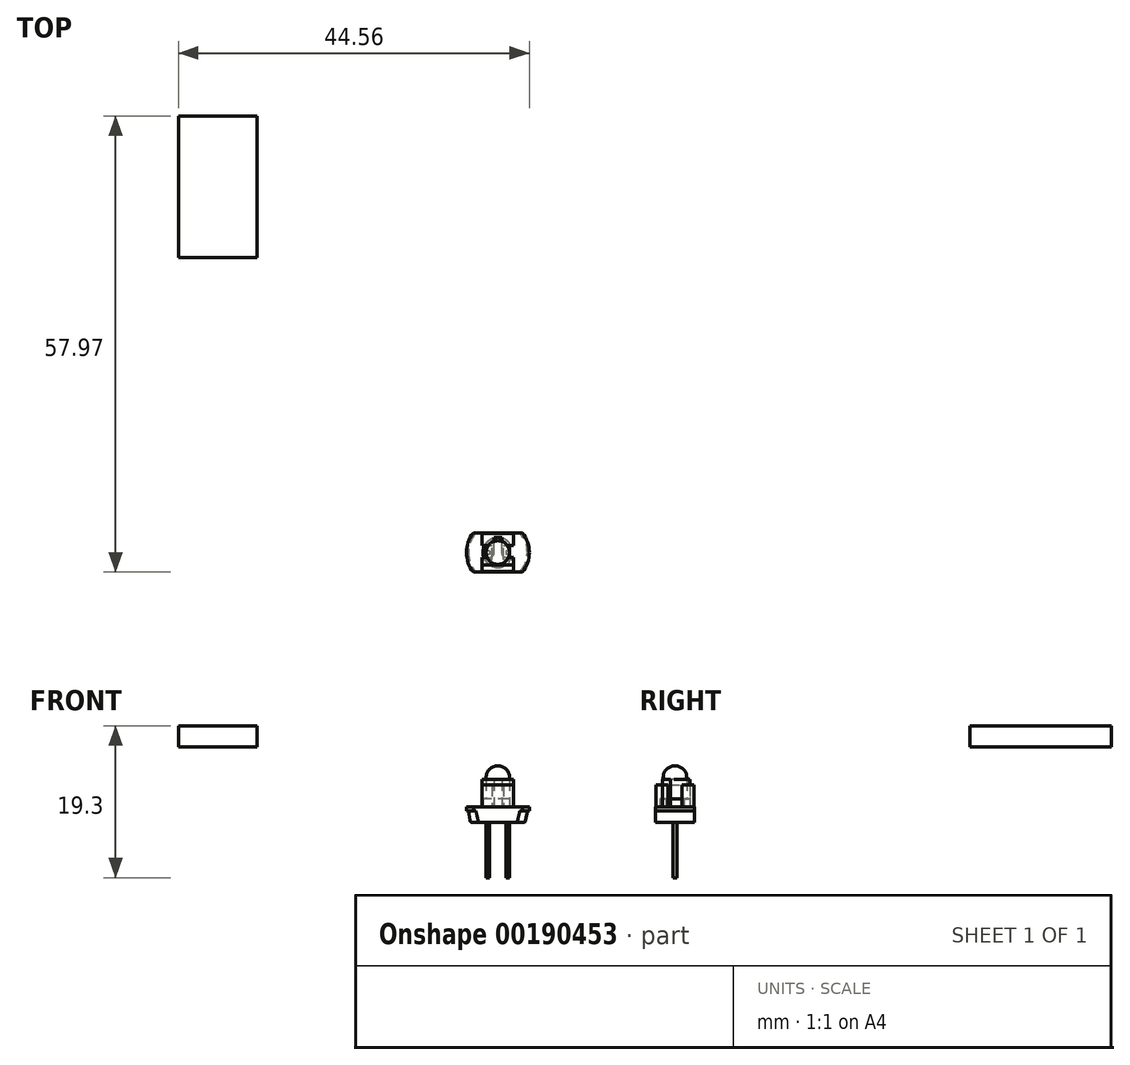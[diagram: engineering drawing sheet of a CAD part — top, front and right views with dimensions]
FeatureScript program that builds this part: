
annotation { "Feature Type Name" : "Feature", "Feature Type Description" : "" }
export const myFeature = defineFeature(function(context is Context, id is Id, definition is map)
    precondition{}
    {
        {
            var Q0;
            Q0=qCreatedBy(makeId("Front.planeOp"),FACE);
            var sketch = newSketch(context, id + "F0", { "sketchPlane" : qUnion([Q0])});
            skLineSegment(sketch, "E0", {"start": v(0, 10.98) * mm, "end": v(0, -8.22) * mm, "construction": true});
            skSolve(sketch);
        }
        {
            var Q0;
            Q0=qCreatedBy(makeId("Top.planeOp"),FACE);
            cPlane(context, id + "F1", {"entities" : qUnion([Q0]), "cplaneType" : CPlaneType.OFFSET, "offset" : 2 * mm, "width" : 150 * mm, "height" : 150 * mm});
        }
        {
            var Q0;
            Q0=qCreatedBy(makeId("Top.planeOp"),FACE);
            var sketch = newSketch(context, id + "F2", { "sketchPlane" : qUnion([Q0])});
            skLineSegment(sketch, "E1", {"start": v(0, 8.57) * mm, "end": v(0, -6.8) * mm, "construction": true});
            skLineSegment(sketch, "E2", {"start": v(-7.73, 0) * mm, "end": v(6.61, 0) * mm, "construction": true});
            skLineSegment(sketch, "E3.bottom", {"start": v(-4.25, 1.75) * mm, "end": v(4.25, 1.75) * mm});
            skLineSegment(sketch, "E3.top", {"start": v(-4.25, -1.75) * mm, "end": v(4.25, -1.75) * mm});
            skLineSegment(sketch, "E3.left", {"start": v(-4.25, 1.75) * mm, "end": v(-4.25, -1.75) * mm});
            skLineSegment(sketch, "E3.right", {"start": v(4.25, 1.75) * mm, "end": v(4.25, -1.75) * mm});
            skSolve(sketch);
        }
        {
            var Q0;
            Q0=qSketchRegion(id+"F2",true);
            extrude(context, id + "F3", {"entities" : qUnion([Q0]), "depth" : 3.5 * mm});
        }
        {
            var Q0;
            Q0=makeQuery(id+"F3.opExtrude","CAP_FACE",FACE,{"disambiguationData":[OSD([sQuery(id+"F2.wireOp",EDGE,"E3.bottom"),sQuery(id+"F2.wireOp",EDGE,"E3.top"),sQuery(id+"F2.wireOp",EDGE,"E3.left"),sQuery(id+"F2.wireOp",EDGE,"E3.right")])],"isStart":false});
            var sketch = newSketch(context, id + "F4", { "sketchPlane" : qUnion([Q0])});
            skLineSegment(sketch, "E4.bottom", {"start": v(-1.75, 0.75) * mm, "end": v(-0.25, 0.75) * mm});
            skLineSegment(sketch, "E4.top", {"start": v(-1.75, -0.75) * mm, "end": v(-0.25, -0.75) * mm});
            skLineSegment(sketch, "E4.left", {"start": v(-1.75, 0.75) * mm, "end": v(-1.75, -0.75) * mm});
            skLineSegment(sketch, "E4.right", {"start": v(-0.25, 0.75) * mm, "end": v(-0.25, -0.75) * mm});
            skLineSegment(sketch, "E5", {"start": v(-2.91, 0) * mm, "end": v(1.63, 0) * mm, "construction": true});
            skSolve(sketch);
        }
        {
            var Q0;
            Q0=qSketchRegion(id+"F4",true);
            extrude(context, id + "F5", {"entities" : qUnion([Q0]), "operationType" : NewBodyOperationType.ADD, "depth" : 2 * mm});
        }
        {
            var Q0;
            Q0=makeQuery(id+"F3.opExtrude","CAP_FACE",FACE,{"disambiguationData":[OSD([sQuery(id+"F2.wireOp",EDGE,"E3.bottom"),sQuery(id+"F2.wireOp",EDGE,"E3.top"),sQuery(id+"F2.wireOp",EDGE,"E3.left"),sQuery(id+"F2.wireOp",EDGE,"E3.right")])],"isStart":true});
            var sketch = newSketch(context, id + "F6", { "sketchPlane" : qUnion([Q0])});
            skLineSegment(sketch, "E6.bottom", {"start": v(-2.8, 2.5) * mm, "end": v(-2.2, 2.5) * mm});
            skLineSegment(sketch, "E6.top", {"start": v(-2.8, 1.75) * mm, "end": v(-2.2, 1.75) * mm});
            skLineSegment(sketch, "E6.left", {"start": v(-2.8, 2.5) * mm, "end": v(-2.8, 1.75) * mm});
            skLineSegment(sketch, "E6.right", {"start": v(-2.2, 2.5) * mm, "end": v(-2.2, 1.75) * mm});
            skLineSegment(sketch, "E7.1.0.0", {"start": v(-0.3, 1.75) * mm, "end": v(0.3, 1.75) * mm});
            skLineSegment(sketch, "E7.1.0.1", {"start": v(-0.3, 2.5) * mm, "end": v(-0.3, 1.75) * mm});
            skLineSegment(sketch, "E7.1.0.2", {"start": v(0.3, 2.5) * mm, "end": v(0.3, 1.75) * mm});
            skLineSegment(sketch, "E7.1.0.3", {"start": v(-0.3, 2.5) * mm, "end": v(0.3, 2.5) * mm});
            skLineSegment(sketch, "E7.2.0.0", {"start": v(2.2, 1.75) * mm, "end": v(2.8, 1.75) * mm});
            skLineSegment(sketch, "E7.2.0.1", {"start": v(2.2, 2.5) * mm, "end": v(2.2, 1.75) * mm});
            skLineSegment(sketch, "E7.2.0.2", {"start": v(2.8, 2.5) * mm, "end": v(2.8, 1.75) * mm});
            skLineSegment(sketch, "E7.2.0.3", {"start": v(2.2, 2.5) * mm, "end": v(2.8, 2.5) * mm});
            skLineSegment(sketch, "E7.direction1", {"start": v(-2.8, 1.75) * mm, "end": v(-0.3, 1.75) * mm, "construction": true});
            skLineSegment(sketch, "E8", {"start": v(-2.83, 0) * mm, "end": v(2.14, 0) * mm, "construction": true});
            skLineSegment(sketch, "E9.0.MirrorCS", {"start": v(2.2, -2.5) * mm, "end": v(2.8, -2.5) * mm});
            skLineSegment(sketch, "E9.1.MirrorCS", {"start": v(-0.3, -2.5) * mm, "end": v(0.3, -2.5) * mm});
            skLineSegment(sketch, "E9.2.MirrorCS", {"start": v(-2.8, -2.5) * mm, "end": v(-2.2, -2.5) * mm});
            skLineSegment(sketch, "E9.3.MirrorCS", {"start": v(2.8, -2.5) * mm, "end": v(2.8, -1.75) * mm});
            skLineSegment(sketch, "E9.4.MirrorCS", {"start": v(2.2, -2.5) * mm, "end": v(2.2, -1.75) * mm});
            skLineSegment(sketch, "E9.5.MirrorCS", {"start": v(0.3, -2.5) * mm, "end": v(0.3, -1.75) * mm});
            skLineSegment(sketch, "E9.6.MirrorCS", {"start": v(-0.3, -2.5) * mm, "end": v(-0.3, -1.75) * mm});
            skLineSegment(sketch, "E9.7.MirrorCS", {"start": v(-2.2, -2.5) * mm, "end": v(-2.2, -1.75) * mm});
            skLineSegment(sketch, "E9.8.MirrorCS", {"start": v(-2.8, -2.5) * mm, "end": v(-2.8, -1.75) * mm});
            skLineSegment(sketch, "E9.9.MirrorCS", {"start": v(2.2, -1.75) * mm, "end": v(2.8, -1.75) * mm});
            skLineSegment(sketch, "E9.10.MirrorCS", {"start": v(-2.8, -1.75) * mm, "end": v(-2.2, -1.75) * mm});
            skLineSegment(sketch, "E9.11.MirrorCS", {"start": v(-0.3, -1.75) * mm, "end": v(0.3, -1.75) * mm});
            skSolve(sketch);
        }
        {
            var Q0;
            Q0=qSketchRegion(id+"F6",true);
            extrude(context, id + "F7", {"entities" : qUnion([Q0]), "operationType" : NewBodyOperationType.ADD, "oppositeDirection" : true, "depth" : 0.3 * mm});
        }
        {
            var Q0;
            Q0=makeQuery(id+"F3.opExtrude","SWEPT_BODY",BODY,{"disambiguationData":[OSD([sQuery(id+"F2.wireOp",EDGE,"E3.bottom"),sQuery(id+"F2.wireOp",EDGE,"E3.top"),sQuery(id+"F2.wireOp",EDGE,"E3.left"),sQuery(id+"F2.wireOp",EDGE,"E3.right")])]});
            transform(context, id + "F8", {"entities" : qUnion([Q0]), "transformType" : TransformType.TRANSLATION_3D, "dx" : -23 * mm, "dy" : 46.3 * mm, "dz" : 7.6 * mm, "makeCopy" : false});
        }
        {
            var Q0;
            Q0=qCreatedBy(makeId("Front.planeOp"),FACE);
            var sketch = newSketch(context, id + "F9", { "sketchPlane" : qUnion([Q0])});
            skLineSegment(sketch, "E10", {"start": v(0, 0) * mm, "end": v(4, 0) * mm});
            skLineSegment(sketch, "E11", {"start": v(4, 0) * mm, "end": v(4, -0.5) * mm});
            skLineSegment(sketch, "E12", {"start": v(4, -0.5) * mm, "end": v(3.75, -0.5) * mm});
            skLineSegment(sketch, "E13", {"start": v(3.75, -0.5) * mm, "end": v(3.54, -1.75) * mm});
            skLineSegment(sketch, "E14", {"start": v(3.25, -2) * mm, "end": v(0, -2) * mm});
            skLineSegment(sketch, "E15", {"start": v(0, -2) * mm, "end": v(0, 0) * mm});
            skPoint(sketch, "E16.visualSharp", {"position": v(3.5, -2) * mm});
            skArc(sketch, "E16.filletArc", {"start": v(3.25, -2) * mm, "mid": v(3.44, -1.93) * mm, "end": v(3.54, -1.75) * mm});
            skSolve(sketch);
        }
        {
            var Q0;
            Q0=qSketchRegion(id+"F9",true);
            var Q1;
            Q1=sQuery(id+"F9.wireOp",EDGE,"E15");
            revolve(context, id + "F10", {"entities" : qUnion([Q0]), "axis" : qUnion([Q1]), "revolveType" : RevolveType.FULL});
        }
        {
            var Q0;
            Q0=qCreatedBy(makeId("Front.planeOp"),FACE);
            var sketch = newSketch(context, id + "F11", { "sketchPlane" : qUnion([Q0])});
            skLineSegment(sketch, "E17", {"start": v(0, 0) * mm, "end": v(4, 0) * mm});
            skLineSegment(sketch, "E18", {"start": v(4, 0) * mm, "end": v(4, -0.5) * mm});
            skLineSegment(sketch, "E19", {"start": v(4, -0.5) * mm, "end": v(3.75, -0.5) * mm});
            skLineSegment(sketch, "E20", {"start": v(3.75, -0.5) * mm, "end": v(3.64, -0.68) * mm});
            skLineSegment(sketch, "E21", {"start": v(0, 0) * mm, "end": v(0, -2) * mm});
            skLineSegment(sketch, "E22", {"start": v(0, -2) * mm, "end": v(0.5, -2) * mm});
            skArc(sketch, "E23", {"start": v(0.5, -2) * mm, "mid": v(2.2, -1.66) * mm, "end": v(3.64, -0.68) * mm});
            skSolve(sketch);
        }
        {
            var Q0;
            Q0=qSketchRegion(id+"F11",true);
            var Q1;
            Q1=sQuery(id+"F11.wireOp",EDGE,"E21");
            revolve(context, id + "F12", {"entities" : qUnion([Q0]), "axis" : qUnion([Q1]), "revolveType" : RevolveType.FULL});
        }
        {
            var Q0;
            Q0=makeQuery(id+"F12.opRevolve","SWEPT_BODY",BODY,{"disambiguationData":[OSD([sQuery(id+"F11.wireOp",EDGE,"E17"),sQuery(id+"F11.wireOp",EDGE,"E18"),sQuery(id+"F11.wireOp",EDGE,"E19"),sQuery(id+"F11.wireOp",EDGE,"E20"),sQuery(id+"F11.wireOp",EDGE,"E21"),sQuery(id+"F11.wireOp",EDGE,"E22"),sQuery(id+"F11.wireOp",EDGE,"E23")])]});
            transform(context, id + "F13", {"entities" : qUnion([Q0]), "transformType" : TransformType.COPY});
        }
        {
            var Q0;
            Q0=makeQuery(id+"F13.opPattern","COPY",FACE,{"derivedFrom":makeQuery(id+"F12.opRevolve","SWEPT_FACE",FACE,{"disambiguationData":[OSD([sQuery(id+"F11.wireOp",EDGE,"E17")])]}),"instanceName":"1"});
            var sketch = newSketch(context, id + "F14", { "sketchPlane" : qUnion([Q0])});
            skLineSegment(sketch, "E24", {"start": v(-3.12, 2.5) * mm, "end": v(3.12, 2.5) * mm});
            skLineSegment(sketch, "E25", {"start": v(-3.12, -2.5) * mm, "end": v(3.12, -2.5) * mm});
            skLineSegment(sketch, "E26", {"start": v(0, 0) * mm, "end": v(3.07, 0) * mm, "construction": true});
            skArc(sketch, "E27.0", {"start": v(-3.12, 2.5) * mm, "mid": v(-4, 0) * mm, "end": v(-3.12, -2.5) * mm});
            skArc(sketch, "E28.trimOffspring", {"start": v(3.12, -2.5) * mm, "mid": v(4, 0) * mm, "end": v(3.12, 2.5) * mm});
            skSolve(sketch);
        }
        {
            var Q0;
            Q0=qSketchRegion(id+"F14",true);
            extrude(context, id + "F15", {"entities" : qUnion([Q0]), "operationType" : NewBodyOperationType.INTERSECT, "oppositeDirection" : true, "depth" : 25 * mm});
        }
        {
            var Q0;
            Q0=qCreatedBy(makeId("Front.planeOp"),FACE);
            var sketch = newSketch(context, id + "F16", { "sketchPlane" : qUnion([Q0])});
            skLineSegment(sketch, "E29", {"start": v(0, 0) * mm, "end": v(0, 5.2) * mm});
            skLineSegment(sketch, "E30", {"start": v(0, 0) * mm, "end": v(1.9, 0) * mm});
            skLineSegment(sketch, "E31", {"start": v(1.9, 0) * mm, "end": v(1.9, 1) * mm});
            skLineSegment(sketch, "E32", {"start": v(1.9, 1) * mm, "end": v(1.5, 1) * mm});
            skLineSegment(sketch, "E33", {"start": v(1.5, 1) * mm, "end": v(1.5, 3.7) * mm});
            skArc(sketch, "E34", {"start": v(1.5, 3.7) * mm, "mid": v(1.06, 4.76) * mm, "end": v(0, 5.2) * mm});
            skLineSegment(sketch, "E35", {"start": v(0, 3.7) * mm, "end": v(1, 3.7) * mm, "construction": true});
            skSolve(sketch);
        }
        {
            var Q0;
            Q0=qSketchRegion(id+"F16",true);
            var Q1;
            Q1=sQuery(id+"F16.wireOp",EDGE,"E29");
            revolve(context, id + "F17", {"entities" : qUnion([Q0]), "axis" : qUnion([Q1]), "revolveType" : RevolveType.FULL});
        }
        {
            var Q0;
            Q0=makeQuery(id+"F17.opRevolve","SWEPT_FACE",FACE,{"disambiguationData":[OSD([sQuery(id+"F16.wireOp",EDGE,"E30")])]});
            var sketch = newSketch(context, id + "F18", { "sketchPlane" : qUnion([Q0])});
            skLineSegment(sketch, "E36.bottom", {"start": v(2.77, -2.04) * mm, "end": v(1.5, -2.04) * mm});
            skLineSegment(sketch, "E36.top", {"start": v(2.77, 2.1) * mm, "end": v(1.5, 2.1) * mm});
            skLineSegment(sketch, "E36.left", {"start": v(2.77, -2.04) * mm, "end": v(2.77, 2.1) * mm});
            skLineSegment(sketch, "E36.right", {"start": v(1.5, -2.04) * mm, "end": v(1.5, 2.1) * mm});
            skSolve(sketch);
        }
        {
            var Q0;
            Q0=qSketchRegion(id+"F18",true);
            extrude(context, id + "F19", {"entities" : qUnion([Q0]), "operationType" : NewBodyOperationType.REMOVE, "oppositeDirection" : true, "depth" : 25 * mm});
        }
        {
            var Q0;
            Q0=makeQuery(id+"F17.opRevolve","SWEPT_FACE",FACE,{"disambiguationData":[OSD([sQuery(id+"F16.wireOp",EDGE,"E30")])]});
            var sketch = newSketch(context, id + "F20", { "sketchPlane" : qUnion([Q0])});
            skLineSegment(sketch, "E37.bottom", {"start": v(-1.05, -0.23) * mm, "end": v(-1.5, -0.22) * mm});
            skLineSegment(sketch, "E37.top", {"start": v(-1.05, 0.23) * mm, "end": v(-1.5, 0.23) * mm});
            skLineSegment(sketch, "E37.left", {"start": v(-1.05, -0.23) * mm, "end": v(-1.05, 0.23) * mm});
            skLineSegment(sketch, "E37.right", {"start": v(-1.5, -0.22) * mm, "end": v(-1.5, 0.23) * mm});
            skPoint(sketch, "E37.middle", {"position": v(-1.27, 0) * mm});
            skLineSegment(sketch, "E38.bottom", {"start": v(1.5, -0.22) * mm, "end": v(1.04, -0.23) * mm});
            skLineSegment(sketch, "E38.top", {"start": v(1.5, 0.23) * mm, "end": v(1.04, 0.23) * mm});
            skLineSegment(sketch, "E38.left", {"start": v(1.5, -0.22) * mm, "end": v(1.5, 0.23) * mm});
            skLineSegment(sketch, "E38.right", {"start": v(1.04, -0.23) * mm, "end": v(1.04, 0.23) * mm});
            skPoint(sketch, "E38.middle", {"position": v(1.27, 0) * mm});
            skSolve(sketch);
        }
        {
            var Q0;
            Q0=qSketchRegion(id+"F20",true);
            extrude(context, id + "F21", {"entities" : qUnion([Q0]), "operationType" : NewBodyOperationType.ADD, "depth" : 9 * mm});
        }
        {
            var Q0;
            Q0=qCreatedBy(makeId("Top.planeOp"),FACE);
            var sketch = newSketch(context, id + "F22", { "sketchPlane" : qUnion([Q0])});
            skLineSegment(sketch, "E39.bottom", {"start": v(-5, 0) * mm, "end": v(5, 0) * mm});
            skLineSegment(sketch, "E39.top", {"start": v(-5, 18) * mm, "end": v(5, 18) * mm});
            skLineSegment(sketch, "E39.left", {"start": v(-5, 0) * mm, "end": v(-5, 18) * mm});
            skLineSegment(sketch, "E39.right", {"start": v(5, 0) * mm, "end": v(5, 18) * mm});
            skPoint(sketch, "E40", {"position": v(0, 0) * mm});
            skSolve(sketch);
        }
        {
            var Q0;
            Q0=qSketchRegion(id+"F22",true);
            extrude(context, id + "F23", {"entities" : qUnion([Q0]), "depth" : 2.7 * mm});
        }
        {
            var Q0;
            Q0=makeQuery(id+"F23.opExtrude","SWEPT_BODY",BODY,{"disambiguationData":[OSD([sQuery(id+"F22.wireOp",EDGE,"E39.bottom"),sQuery(id+"F22.wireOp",EDGE,"E39.top"),sQuery(id+"F22.wireOp",EDGE,"E39.left"),sQuery(id+"F22.wireOp",EDGE,"E39.right")])]});
            transform(context, id + "F24", {"entities" : qUnion([Q0]), "transformType" : TransformType.TRANSLATION_3D, "dx" : -35.56 * mm, "dy" : 37.47 * mm, "dz" : 7.6 * mm, "makeCopy" : false});
        }
        {
            var Q0;
            Q0=qCreatedBy(makeId("Top.planeOp"),FACE);
            var sketch = newSketch(context, id + "F25", { "sketchPlane" : qUnion([Q0])});
            skLineSegment(sketch, "E41.bottom", {"start": v(-0.75, -2.4) * mm, "end": v(0.75, -2.4) * mm});
            skLineSegment(sketch, "E41.top", {"start": v(-0.75, 2.4) * mm, "end": v(0.75, 2.4) * mm});
            skLineSegment(sketch, "E41.left", {"start": v(-0.75, -2.4) * mm, "end": v(-0.75, 2.4) * mm});
            skLineSegment(sketch, "E41.right", {"start": v(0.75, -2.4) * mm, "end": v(0.75, 2.4) * mm});
            skLineSegment(sketch, "E42.bottom", {"start": v(-2, -0.9) * mm, "end": v(2, -0.9) * mm});
            skLineSegment(sketch, "E42.top", {"start": v(-2, -2.4) * mm, "end": v(2, -2.4) * mm});
            skLineSegment(sketch, "E42.left", {"start": v(-2, -0.9) * mm, "end": v(-2, -2.4) * mm});
            skLineSegment(sketch, "E42.right", {"start": v(2, -0.9) * mm, "end": v(2, -2.4) * mm});
            skLineSegment(sketch, "E43.bottom", {"start": v(-2, 2.4) * mm, "end": v(2, 2.4) * mm});
            skLineSegment(sketch, "E43.top", {"start": v(-2, 0.9) * mm, "end": v(2, 0.9) * mm});
            skLineSegment(sketch, "E43.left", {"start": v(-2, 2.4) * mm, "end": v(-2, 0.9) * mm});
            skLineSegment(sketch, "E43.right", {"start": v(2, 2.4) * mm, "end": v(2, 0.9) * mm});
            skPoint(sketch, "E44", {"position": v(0, -2.4) * mm});
            skSolve(sketch);
        }
        {
            var Q0;
            Q0=qSketchRegion(id+"F25",true);
            extrude(context, id + "F26", {"entities" : qUnion([Q0]), "depth" : 2.8 * mm});
        }
        {
            var Q0;
            Q0=qCreatedBy(makeId("Top.planeOp"),FACE);
            var sketch = newSketch(context, id + "F27", { "sketchPlane" : qUnion([Q0])});
            skLineSegment(sketch, "E45.bottom", {"start": v(-2, -0.6) * mm, "end": v(2, -0.6) * mm});
            skLineSegment(sketch, "E45.top", {"start": v(-2, -1.6) * mm, "end": v(2, -1.6) * mm});
            skLineSegment(sketch, "E45.left", {"start": v(-2, -0.6) * mm, "end": v(-2, -1.6) * mm});
            skLineSegment(sketch, "E45.right", {"start": v(2, -0.6) * mm, "end": v(2, -1.6) * mm});
            skLineSegment(sketch, "E46.bottom", {"start": v(-0.5, -0.6) * mm, "end": v(0.5, -0.6) * mm});
            skLineSegment(sketch, "E46.top", {"start": v(-0.5, 1.9) * mm, "end": v(0.5, 1.9) * mm});
            skLineSegment(sketch, "E46.left", {"start": v(-0.5, -0.6) * mm, "end": v(-0.5, 1.9) * mm});
            skLineSegment(sketch, "E46.right", {"start": v(0.5, -0.6) * mm, "end": v(0.5, 1.9) * mm});
            skLineSegment(sketch, "E47", {"start": v(0, 0) * mm, "end": v(0, 0.95) * mm, "construction": true});
            skSolve(sketch);
        }
        {
            var Q0;
            Q0=qSketchRegion(id+"F27",true);
            extrude(context, id + "F28", {"entities" : qUnion([Q0]), "depth" : 3.5 * mm});
        }
        {
            var Q0;
            Q0=makeQuery(id+"F28.opExtrude","SWEPT_EDGE",EDGE,{"disambiguationData":[OSD([sQuery(id+"F27.wireOp",EDGE,"E45.bottom"),sQuery(id+"F27.wireOp",EDGE,"E46.bottom"),sQuery(id+"F27.wireOp",EDGE,"E46.left")])]});
            var Q1;
            Q1=makeQuery(id+"F28.opExtrude","SWEPT_EDGE",EDGE,{"disambiguationData":[OSD([sQuery(id+"F27.wireOp",EDGE,"E45.bottom"),sQuery(id+"F27.wireOp",EDGE,"E46.bottom"),sQuery(id+"F27.wireOp",EDGE,"E46.right")])]});
            fillet(context, id + "F29", {"entities" : qUnion([Q0, Q1]), "radius" : 0.5 * mm, "tangentPropagation" : true, "allowEdgeOverflow" : false});
        }
    });
